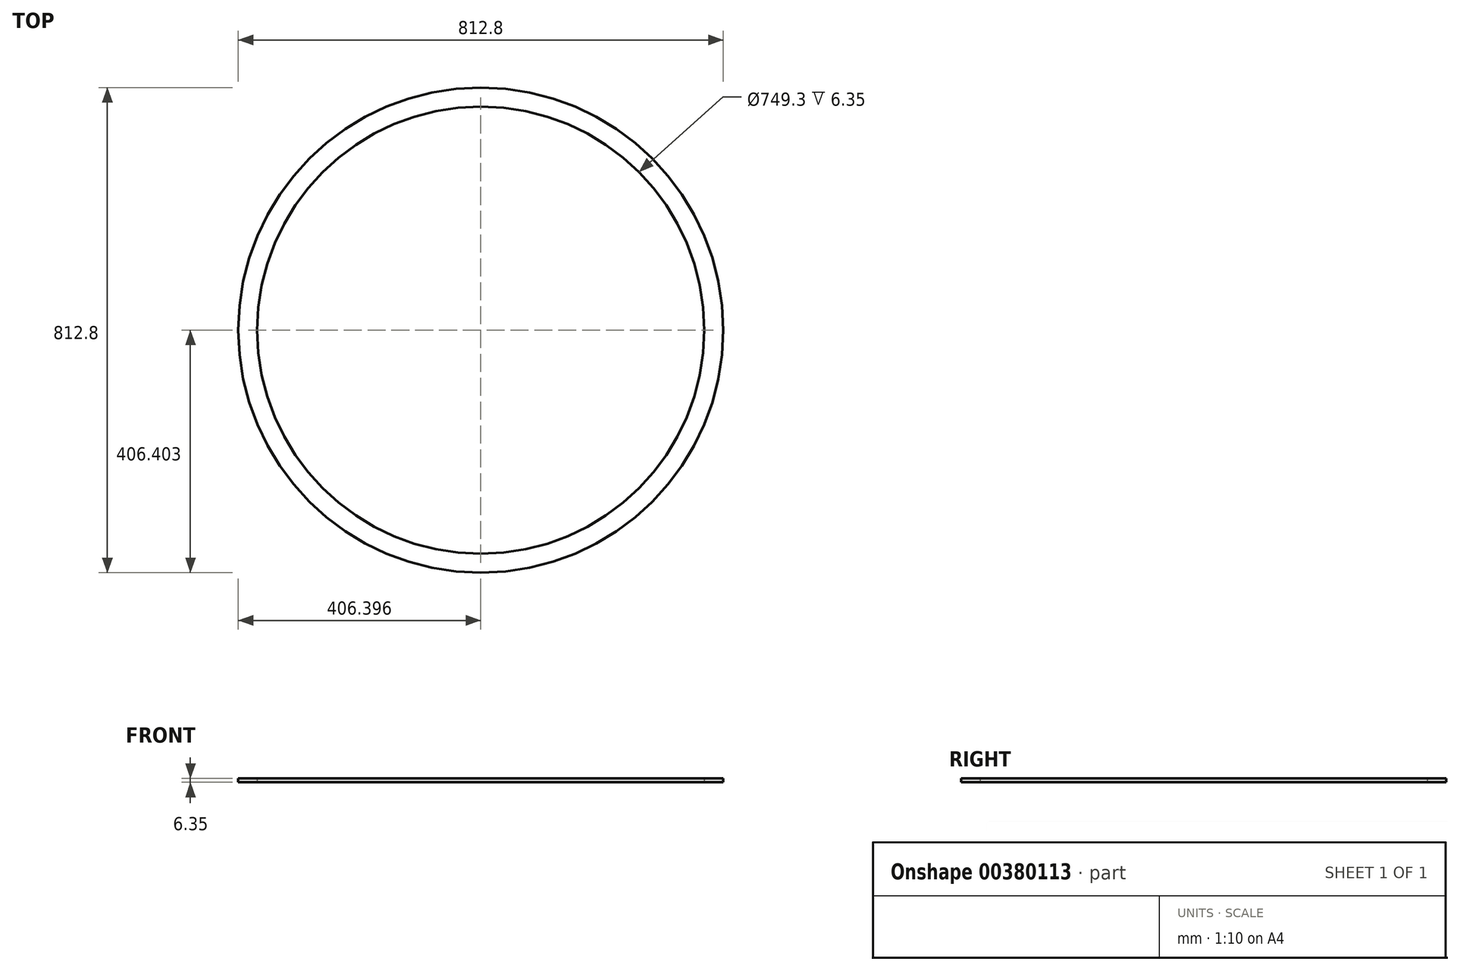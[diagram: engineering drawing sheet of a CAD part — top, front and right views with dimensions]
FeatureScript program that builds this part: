
annotation { "Feature Type Name" : "Feature", "Feature Type Description" : "" }
export const myFeature = defineFeature(function(context is Context, id is Id, definition is map)
    precondition{}
    {
        {
            var Q0;
            Q0=qCreatedBy(makeId("Top.planeOp"),FACE);
            var sketch = newSketch(context, id + "F0", { "sketchPlane" : qUnion([Q0])});
            skCircle(sketch, "E0", {"center": v(-4.6, 18) * mm, "radius": 457.2 * mm});
            skCircle(sketch, "E1", {"center": v(-4.6, 18) * mm, "radius": 3.18 * mm});
            skCircle(sketch, "E2", {"center": v(-4.6, 18) * mm, "radius": 406.4 * mm});
            skCircle(sketch, "E3", {"center": v(-4.6, 18) * mm, "radius": 374.65 * mm});
            skSolve(sketch);
        }
        {
            var Q0;
            Q0=makeQuery(id+"F0.imprint","IMPRINT",FACE,{"disambiguationData":[TD([[makeQuery(id+"F0.imprint","IMPRINT",EDGE,{"derivedFrom":sQuery(id+"F0.wireOp",EDGE,"E2")}),1.0]])]});
            extrude(context, id + "F1", {"entities" : qUnion([Q0]), "depth" : 6.35 * mm});
        }
    });
